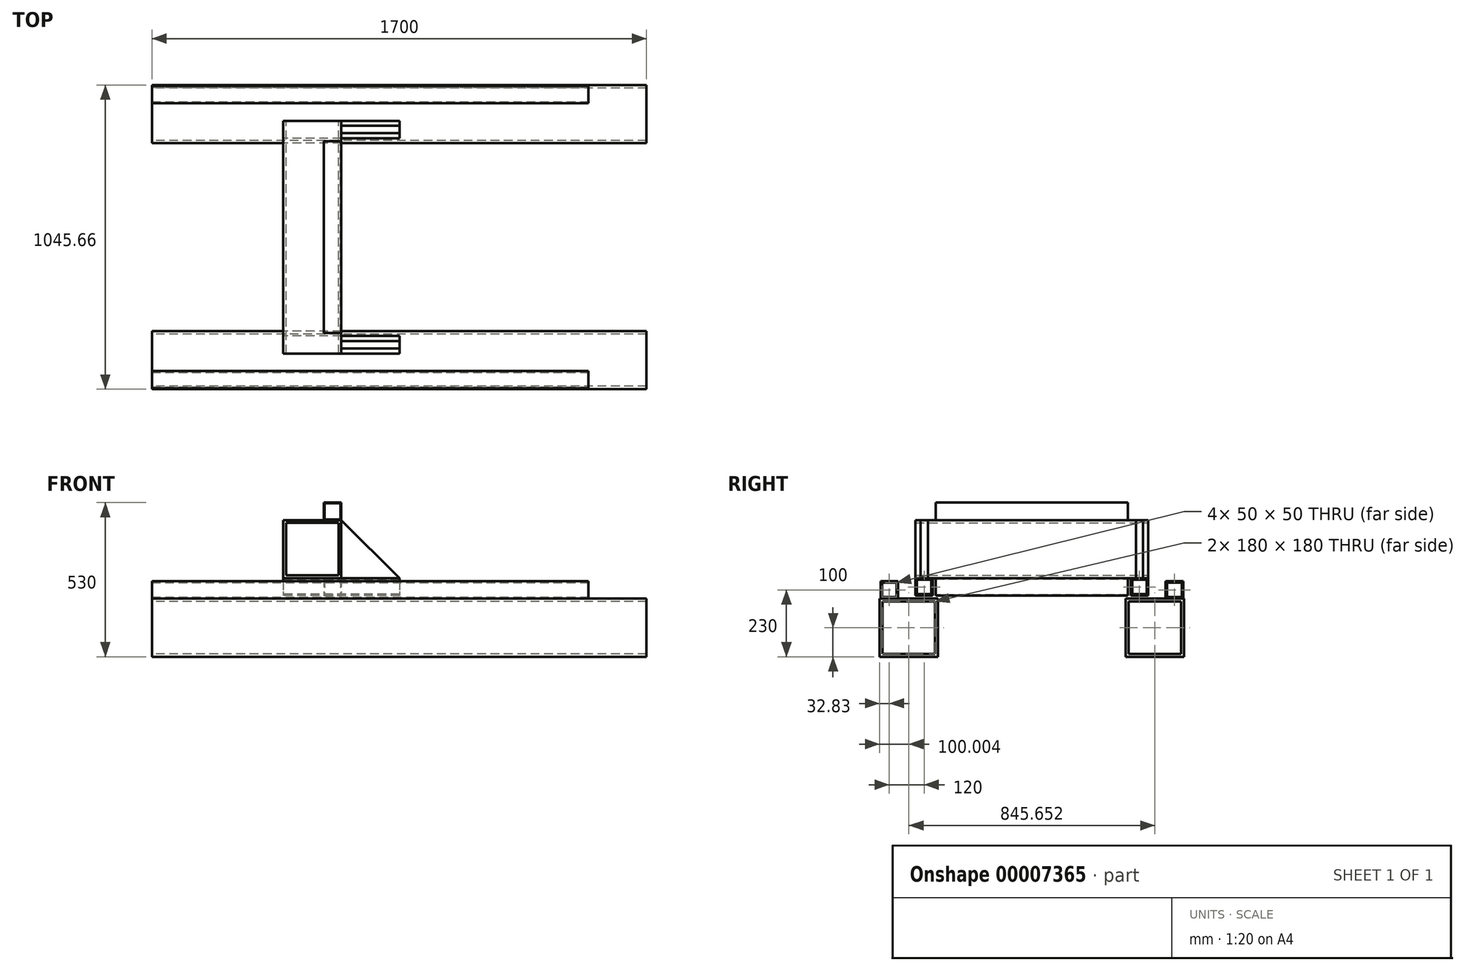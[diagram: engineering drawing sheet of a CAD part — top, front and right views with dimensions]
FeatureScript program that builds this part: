
annotation { "Feature Type Name" : "Feature", "Feature Type Description" : "" }
export const myFeature = defineFeature(function(context is Context, id is Id, definition is map)
    precondition{}
    {
        {
            var Q0;
            Q0=qCreatedBy(makeId("Front.planeOp"),FACE);
            var sketch = newSketch(context, id + "F0", { "sketchPlane" : qUnion([Q0])});
            skLineSegment(sketch, "E0.bottom", {"start": v(0, 0) * mm, "end": v(200, 0) * mm});
            skLineSegment(sketch, "E0.top", {"start": v(0, 200) * mm, "end": v(200, 200) * mm});
            skLineSegment(sketch, "E0.left", {"start": v(0, 0) * mm, "end": v(0, 200) * mm});
            skLineSegment(sketch, "E0.right", {"start": v(200, 0) * mm, "end": v(200, 200) * mm});
            skSolve(sketch);
        }
        {
            var Q0;
            Q0 = qSketchRegion(id + "F0", true);
            extrude(context, id + "F1", {"entities" : qUnion([Q0]), "depth" : 800 * mm});
        }
        {
            var Q0;
            Q0=makeQuery(id+"F1.opExtrude","SWEPT_FACE",FACE,{"disambiguationData":[OSD([sQuery(id+"F0.wireOp",EDGE,"E0.left")])]});
            var sketch = newSketch(context, id + "F2", { "sketchPlane" : qUnion([Q0])});
            skLineSegment(sketch, "E1.bottom", {"start": v(0, 0) * mm, "end": v(60, 0) * mm});
            skLineSegment(sketch, "E1.top", {"start": v(0, -60) * mm, "end": v(60, -60) * mm});
            skLineSegment(sketch, "E1.left", {"start": v(0, 0) * mm, "end": v(0, -60) * mm});
            skLineSegment(sketch, "E1.right", {"start": v(60, 0) * mm, "end": v(60, -60) * mm});
            skSolve(sketch);
        }
        {
            var Q0;
            Q0 = qSketchRegion(id + "F2", true);
            extrude(context, id + "F3", {"entities" : qUnion([Q0]), "oppositeDirection" : true, "depth" : 400 * mm});
        }
        {
            var Q0;
            Q0=makeQuery(id+"F3.opExtrude","SWEPT_FACE",FACE,{"disambiguationData":[OSD([sQuery(id+"F2.wireOp",EDGE,"E1.left")])]});
            var Q1;
            Q1=makeQuery(id+"F3.opExtrude","SWEPT_FACE",FACE,{"disambiguationData":[OSD([sQuery(id+"F2.wireOp",EDGE,"E1.right")])]});
            cPlane(context, id + "F4", {"entities" : qUnion([Q0, Q1]), "cplaneType" : CPlaneType.MID_PLANE, "offset" : 25 * mm, "width" : 150 * mm, "height" : 150 * mm});
        }
        {
            var Q0;
            Q0=qCreatedBy(id+"F4.planeOp",FACE);
            var sketch = newSketch(context, id + "F5", { "sketchPlane" : qUnion([Q0])});
            skLineSegment(sketch, "E2", {"start": v(-200, 200) * mm, "end": v(-400, 0) * mm});
            skLineSegment(sketch, "E3", {"start": v(-400, 0) * mm, "end": v(-200, 0) * mm});
            skLineSegment(sketch, "E4", {"start": v(-200, 0) * mm, "end": v(-200, 200) * mm});
            skSolve(sketch);
        }
        {
            var Q0;
            Q0 = qSketchRegion(id + "F5", true);
            extrude(context, id + "F6", {"entities" : qUnion([Q0]), "endBound" : BoundingType.SYMMETRIC, "depth" : 25 * mm});
        }
        {
            var Q0;
            Q0=makeQuery(id+"F1.opExtrude","CAP_FACE",FACE,{"disambiguationData":[OSD([sQuery(id+"F0.wireOp",EDGE,"E0.bottom"),sQuery(id+"F0.wireOp",EDGE,"E0.top"),sQuery(id+"F0.wireOp",EDGE,"E0.left"),sQuery(id+"F0.wireOp",EDGE,"E0.right")])],"isStart":true});
            var Q1;
            Q1=makeQuery(id+"F1.opExtrude","CAP_FACE",FACE,{"disambiguationData":[OSD([sQuery(id+"F0.wireOp",EDGE,"E0.bottom"),sQuery(id+"F0.wireOp",EDGE,"E0.top"),sQuery(id+"F0.wireOp",EDGE,"E0.left"),sQuery(id+"F0.wireOp",EDGE,"E0.right")])],"isStart":false});
            shell(context, id + "F7", {"entities" : qUnion([Q0, Q1]), "thickness" : 10 * mm});
        }
        {
            var Q0;
            Q0=makeQuery(id+"F3.opExtrude","CAP_FACE",FACE,{"disambiguationData":[OSD([sQuery(id+"F2.wireOp",EDGE,"E1.bottom"),sQuery(id+"F2.wireOp",EDGE,"E1.top"),sQuery(id+"F2.wireOp",EDGE,"E1.left"),sQuery(id+"F2.wireOp",EDGE,"E1.right")])],"isStart":true});
            var Q1;
            Q1=makeQuery(id+"F3.opExtrude","CAP_FACE",FACE,{"disambiguationData":[OSD([sQuery(id+"F2.wireOp",EDGE,"E1.bottom"),sQuery(id+"F2.wireOp",EDGE,"E1.top"),sQuery(id+"F2.wireOp",EDGE,"E1.left"),sQuery(id+"F2.wireOp",EDGE,"E1.right")])],"isStart":false});
            shell(context, id + "F8", {"entities" : qUnion([Q0, Q1]), "thickness" : 5 * mm});
        }
        {
            var Q0;
            Q0=makeQuery(id+"F1.opExtrude","CAP_FACE",FACE,{"disambiguationData":[OSD([sQuery(id+"F0.wireOp",EDGE,"E0.bottom"),sQuery(id+"F0.wireOp",EDGE,"E0.top"),sQuery(id+"F0.wireOp",EDGE,"E0.left"),sQuery(id+"F0.wireOp",EDGE,"E0.right")])],"isStart":true});
            var Q1;
            Q1=makeQuery(id+"F1.opExtrude","CAP_FACE",FACE,{"disambiguationData":[OSD([sQuery(id+"F0.wireOp",EDGE,"E0.bottom"),sQuery(id+"F0.wireOp",EDGE,"E0.top"),sQuery(id+"F0.wireOp",EDGE,"E0.left"),sQuery(id+"F0.wireOp",EDGE,"E0.right")])],"isStart":false});
            cPlane(context, id + "F9", {"entities" : qUnion([Q0, Q1]), "cplaneType" : CPlaneType.MID_PLANE, "offset" : 25 * mm, "width" : 150 * mm, "height" : 150 * mm});
        }
        {
            var Q0;
            Q0=makeQuery(id+"F1.opExtrude","SWEPT_FACE",FACE,{"disambiguationData":[OSD([sQuery(id+"F0.wireOp",EDGE,"E0.right")])]});
            var sketch = newSketch(context, id + "F10", { "sketchPlane" : qUnion([Q0])});
            skLineSegment(sketch, "E5.bottom", {"start": v(-70, 0) * mm, "end": v(-730, 0) * mm});
            skLineSegment(sketch, "E5.top", {"start": v(-70, -60) * mm, "end": v(-730, -60) * mm});
            skLineSegment(sketch, "E5.left", {"start": v(-70, 0) * mm, "end": v(-70, -60) * mm});
            skLineSegment(sketch, "E5.right", {"start": v(-730, 0) * mm, "end": v(-730, -60) * mm});
            skLineSegment(sketch, "E6", {"start": v(-400, 0) * mm, "end": v(-400, -60) * mm, "construction": true});
            skSolve(sketch);
        }
        {
            var Q0;
            Q0 = qSketchRegion(id + "F10", true);
            extrude(context, id + "F11", {"entities" : qUnion([Q0]), "oppositeDirection" : true, "depth" : 60 * mm});
        }
        {
            var Q0;
            Q0=makeQuery(id+"F11.opExtrude","SWEPT_FACE",FACE,{"disambiguationData":[OSD([sQuery(id+"F10.wireOp",EDGE,"E5.left")])]});
            var Q1;
            Q1=makeQuery(id+"F11.opExtrude","SWEPT_FACE",FACE,{"disambiguationData":[OSD([sQuery(id+"F10.wireOp",EDGE,"E5.right")])]});
            shell(context, id + "F12", {"entities" : qUnion([Q0, Q1]), "thickness" : 2.5 * mm});
        }
        {
            var Q0;
            Q0=makeQuery(id+"F7.opShell","OFFSET_FACE",FACE,{"disambiguationData":[OSD([sQuery(id+"F0.wireOp",EDGE,"E0.bottom")])]});
            var Q1;
            Q1=makeQuery(id+"F7.opShell","OFFSET_FACE",FACE,{"disambiguationData":[OSD([sQuery(id+"F0.wireOp",EDGE,"E0.top")])]});
            cPlane(context, id + "F13", {"entities" : qUnion([Q0, Q1]), "cplaneType" : CPlaneType.MID_PLANE, "offset" : 25 * mm, "width" : 150 * mm, "height" : 150 * mm});
        }
        {
            var Q0;
            Q0=makeQuery(id+"F11.opExtrude","SWEPT_BODY",BODY,{"disambiguationData":[OSD([sQuery(id+"F10.wireOp",EDGE,"E5.bottom"),sQuery(id+"F10.wireOp",EDGE,"E5.top"),sQuery(id+"F10.wireOp",EDGE,"E5.left"),sQuery(id+"F10.wireOp",EDGE,"E5.right")])]});
            var Q1;
            Q1=qCreatedBy(id+"F13.planeOp",FACE);
            mirror(context, id + "F14", {"entities" : qUnion([Q0]), "mirrorPlane" : qUnion([Q1])});
        }
        {
            var Q0;
            Q0=makeQuery(id+"F3.opExtrude","SWEPT_FACE",FACE,{"disambiguationData":[OSD([sQuery(id+"F2.wireOp",EDGE,"E1.top")])]});
            cPlane(context, id + "F15", {"entities" : qUnion([Q0]), "cplaneType" : CPlaneType.OFFSET, "offset" : 10 * mm, "width" : 150 * mm, "height" : 150 * mm});
        }
        {
            var Q0;
            Q0=qCreatedBy(id+"F15.planeOp",FACE);
            var sketch = newSketch(context, id + "F16", { "sketchPlane" : qUnion([Q0])});
            skLineSegment(sketch, "E7.bottom", {"start": v(-451.28, -60) * mm, "end": v(1048.72, -60) * mm});
            skLineSegment(sketch, "E7.top", {"start": v(-451.28, -120) * mm, "end": v(1048.72, -120) * mm});
            skLineSegment(sketch, "E7.left", {"start": v(-451.28, -60) * mm, "end": v(-451.28, -120) * mm});
            skLineSegment(sketch, "E7.right", {"start": v(1048.72, -60) * mm, "end": v(1048.72, -120) * mm});
            skSolve(sketch);
        }
        {
            var Q0;
            Q0=makeQuery(id+"F16.imprint","IMPRINT",FACE,{"disambiguationData":[TD([[makeQuery(id+"F16.imprint","IMPRINT",EDGE,{"derivedFrom":sQuery(id+"F16.wireOp",EDGE,"E7.bottom")}),-1.0]])]});
            extrude(context, id + "F17", {"entities" : qUnion([Q0]), "oppositeDirection" : true, "depth" : 60 * mm});
        }
        {
            var Q0;
            Q0=makeQuery(id+"F17.opExtrude","SWEPT_FACE",FACE,{"disambiguationData":[OSD([sQuery(id+"F16.wireOp",EDGE,"E7.right")])]});
            var Q1;
            Q1=makeQuery(id+"F17.opExtrude","SWEPT_FACE",FACE,{"disambiguationData":[OSD([sQuery(id+"F16.wireOp",EDGE,"E7.left")])]});
            shell(context, id + "F18", {"entities" : qUnion([Q0, Q1]), "thickness" : 5 * mm});
        }
        {
            var Q0;
            Q0=qCreatedBy(id+"F15.planeOp",FACE);
            var sketch = newSketch(context, id + "F19", { "sketchPlane" : qUnion([Q0])});
            skLineSegment(sketch, "E8.bottom", {"start": v(1248.72, 77.17) * mm, "end": v(-451.28, 77.17) * mm});
            skLineSegment(sketch, "E8.top", {"start": v(1248.72, -122.83) * mm, "end": v(-451.28, -122.83) * mm});
            skLineSegment(sketch, "E8.left", {"start": v(1248.72, 77.17) * mm, "end": v(1248.72, -122.83) * mm});
            skLineSegment(sketch, "E8.right", {"start": v(-451.28, 77.17) * mm, "end": v(-451.28, -122.83) * mm});
            skSolve(sketch);
        }
        {
            var Q0;
            Q0 = qSketchRegion(id + "F19", true);
            extrude(context, id + "F20", {"entities" : qUnion([Q0]), "depth" : 200 * mm});
        }
        {
            var Q0;
            Q0=makeQuery(id+"F20.opExtrude","SWEPT_FACE",FACE,{"disambiguationData":[OSD([sQuery(id+"F19.wireOp",EDGE,"E8.right")])]});
            var Q1;
            Q1=makeQuery(id+"F20.opExtrude","SWEPT_FACE",FACE,{"disambiguationData":[OSD([sQuery(id+"F19.wireOp",EDGE,"E8.left")])]});
            shell(context, id + "F21", {"entities" : qUnion([Q0, Q1]), "thickness" : 10 * mm});
        }
        {
            var Q0;
            Q0=makeQuery(id+"F6.opExtrude","SWEPT_BODY",BODY,{"disambiguationData":[OSD([sQuery(id+"F5.wireOp",EDGE,"E2"),sQuery(id+"F5.wireOp",EDGE,"E3"),sQuery(id+"F5.wireOp",EDGE,"E4")])]});
            var Q1;
            Q1=makeQuery(id+"F3.opExtrude","SWEPT_BODY",BODY,{"disambiguationData":[OSD([sQuery(id+"F2.wireOp",EDGE,"E1.bottom"),sQuery(id+"F2.wireOp",EDGE,"E1.top"),sQuery(id+"F2.wireOp",EDGE,"E1.left"),sQuery(id+"F2.wireOp",EDGE,"E1.right")])]});
            var Q2;
            Q2=makeQuery(id+"F20.opExtrude","SWEPT_BODY",BODY,{"disambiguationData":[OSD([sQuery(id+"F19.wireOp",EDGE,"E8.bottom"),sQuery(id+"F19.wireOp",EDGE,"E8.top"),sQuery(id+"F19.wireOp",EDGE,"E8.left"),sQuery(id+"F19.wireOp",EDGE,"E8.right")])]});
            var Q3;
            Q3=makeQuery(id+"F17.opExtrude","SWEPT_BODY",BODY,{"disambiguationData":[OSD([sQuery(id+"F16.wireOp",EDGE,"E7.bottom"),sQuery(id+"F16.wireOp",EDGE,"E7.top"),sQuery(id+"F16.wireOp",EDGE,"E7.left"),sQuery(id+"F16.wireOp",EDGE,"E7.right")])]});
            var Q4;
            Q4=qCreatedBy(id+"F9.planeOp",FACE);
            mirror(context, id + "F22", {"entities" : qUnion([Q0, Q1, Q2, Q3]), "mirrorPlane" : qUnion([Q4])});
        }
    });
